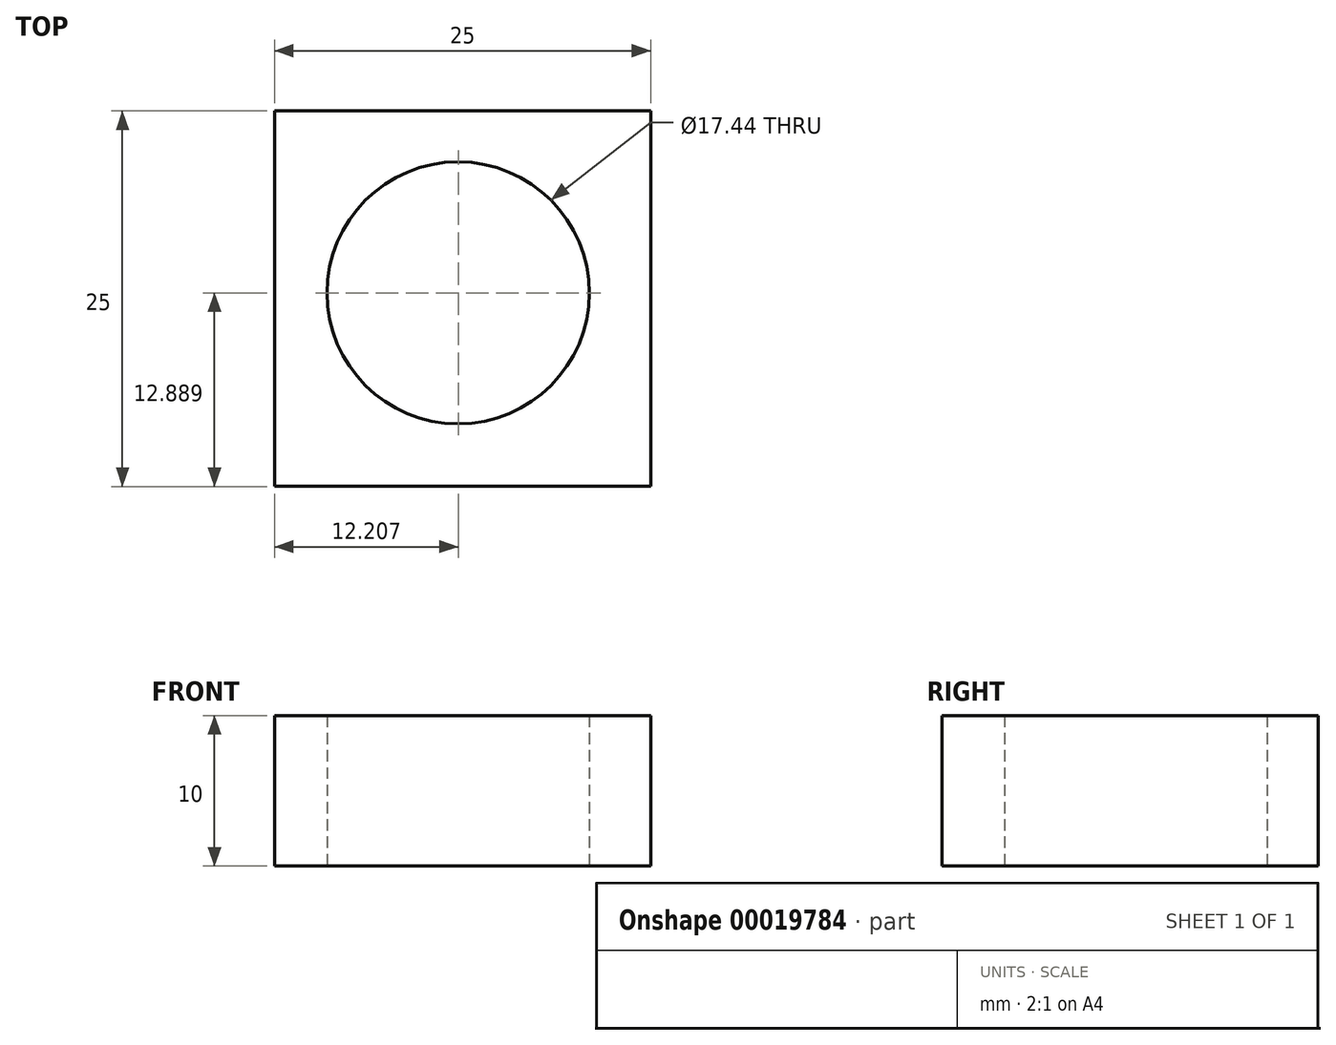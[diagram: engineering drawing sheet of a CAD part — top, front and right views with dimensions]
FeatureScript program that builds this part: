
annotation { "Feature Type Name" : "Feature", "Feature Type Description" : "" }
export const myFeature = defineFeature(function(context is Context, id is Id, definition is map)
    precondition{}
    {
        {
            var Q0;
            Q0=qCreatedBy(makeId("Top.planeOp"),FACE);
            var sketch = newSketch(context, id + "F0", { "sketchPlane" : qUnion([Q0])});
            skLineSegment(sketch, "E0", {"start": v(-14.59, 30.88) * mm, "end": v(10.41, 30.88) * mm});
            skLineSegment(sketch, "E1", {"start": v(10.41, 30.88) * mm, "end": v(10.41, 5.88) * mm});
            skLineSegment(sketch, "E2", {"start": v(10.41, 5.88) * mm, "end": v(-14.59, 5.88) * mm});
            skLineSegment(sketch, "E3", {"start": v(-14.59, 30.88) * mm, "end": v(-14.59, 5.88) * mm});
            skCircle(sketch, "E4", {"center": v(-2.38, 18.77) * mm, "radius": 8.72 * mm});
            skSolve(sketch);
        }
        {
            var Q0;
            Q0 = qSketchRegion(id + "F0", true);
            extrude(context, id + "F1", {"entities" : qUnion([Q0]), "depth" : 10 * mm});
        }
    });
